# Revit family: 422901001_Lavamanos Avanti con Pedestal Blanco
name_source: partatom
category: Plumbing Fixtures
units: mm (PartAtom-declared; Revit-internal decimal feet)

## family parameters
Always vertical = Yes
Cut with Voids When Loaded = No
Host = Wall
OmniClass Number = 23.31.13.11
OmniClass Title = Single Sinks
Part Type = Normal
Room Calculation Point = No
Round Connector Dimension = Use Diameter
Shared = No

## types (1)
- Type 1
    Agujeros para grifería = 35 mm - 1 3/8 pulg.
    Alto = 165 mm  [stored 0.541339 ft]
    Altura = 805 mm  [stored 2.64108 ft]
    Ancho = 505 mm  [stored 1.65682 ft]
    Creado por = IDD
    Description = Lavamanos con funciona diseño contemporáneo ideal para espacios reducidos. Cuenta con agujeros insinuados que permiten escoger diferentes opciones de grifería
    Dimensiones del producto = 660 x 150 x 190 mm
    Fecha de creación = 12/08/2020
    Garantía = Garantía de por vida
    Manufacturer = Corona
    Material = Corona_Porcelana_Sanitaria
    Model = Avanti
    Normas aplicadas = Icontec NTC 920 y ASME/ANSU A112.19.2
    Peso = 11.2 Kg - 24.6 lb
    Peso del producto empacado = 42290: 12 Kg - 26.4 lb
    Profundidad = 430 mm  [stored 1.41076 ft]
    Referencia = 42290
    Referencia pedestal = 04120
    URL = https://www.corona.co

note: [stored X ft] marks values corroborated as IEEE doubles in the binary element streams (Revit-internal decimal feet)

## geometry (parser evidence)
native form markers: Sweep x11
no freeform markers — native parametric forms only
